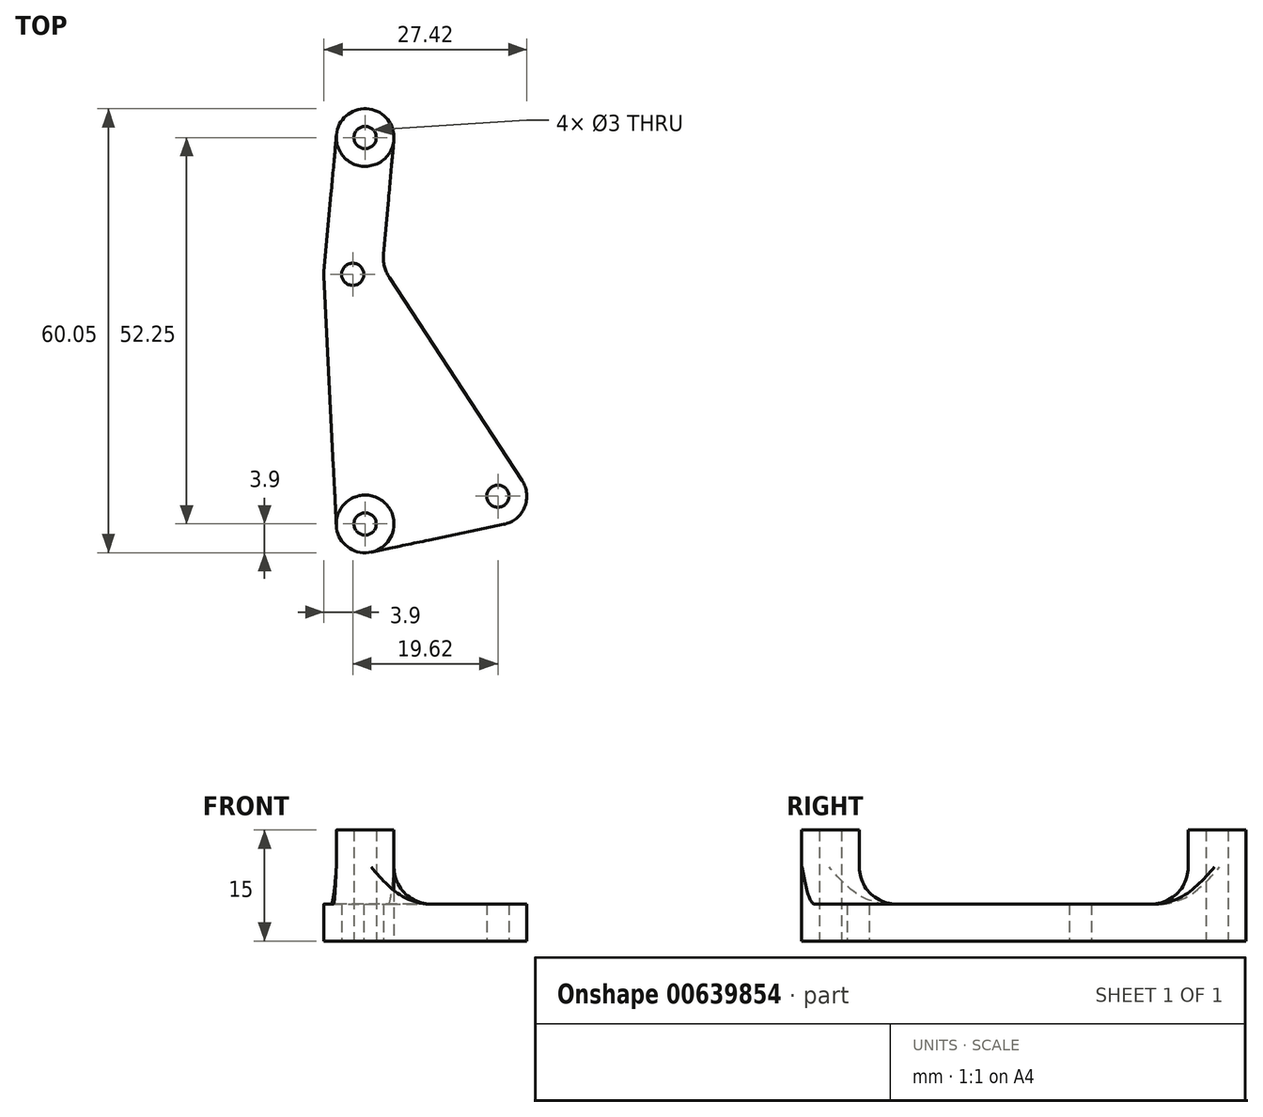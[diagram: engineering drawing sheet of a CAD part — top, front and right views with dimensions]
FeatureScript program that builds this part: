
annotation { "Feature Type Name" : "Feature", "Feature Type Description" : "" }
export const myFeature = defineFeature(function(context is Context, id is Id, definition is map)
    precondition{}
    {
        {
            var Q0;
            Q0=qCreatedBy(makeId("Top.planeOp"),FACE);
            var sketch = newSketch(context, id + "F0", { "sketchPlane" : qUnion([Q0])});
            skCircle(sketch, "E0", {"center": v(-46.5, 15) * mm, "radius": 1.5 * mm});
            skCircle(sketch, "E1", {"center": v(46.5, 15) * mm, "radius": 1.5 * mm});
            skCircle(sketch, "E2", {"center": v(-26.88, -15) * mm, "radius": 1.5 * mm});
            skCircle(sketch, "E3", {"center": v(27.12, -15) * mm, "radius": 1.5 * mm});
            skLineSegment(sketch, "E4.bottom", {"start": v(-47.08, 35.75) * mm, "end": v(47.08, 35.75) * mm, "construction": true});
            skLineSegment(sketch, "E4.top", {"start": v(-47.08, -21) * mm, "end": v(47.07, -21) * mm, "construction": true});
            skLineSegment(sketch, "E4.left", {"start": v(-47.08, 35.75) * mm, "end": v(-47.08, -21) * mm, "construction": true});
            skLineSegment(sketch, "E4.right", {"start": v(47.08, 35.75) * mm, "end": v(47.08, -21) * mm, "construction": true});
            skCircle(sketch, "E5", {"center": v(-44.83, 33.5) * mm, "radius": 1.5 * mm});
            skCircle(sketch, "E6", {"center": v(44.83, 33.5) * mm, "radius": 1.5 * mm});
            skCircle(sketch, "E7", {"center": v(44.82, -18.75) * mm, "radius": 1.5 * mm});
            skCircle(sketch, "E8", {"center": v(-44.83, -18.75) * mm, "radius": 1.5 * mm});
            skCircle(sketch, "E9", {"center": v(-44.83, 33.5) * mm, "radius": 3.9 * mm});
            skCircle(sketch, "E10", {"center": v(44.83, 33.5) * mm, "radius": 3.9 * mm});
            skCircle(sketch, "E11", {"center": v(44.82, -18.75) * mm, "radius": 3.9 * mm});
            skCircle(sketch, "E12", {"center": v(-44.83, -18.75) * mm, "radius": 3.9 * mm});
            skCircle(sketch, "E13", {"center": v(27.12, -15) * mm, "radius": 3.9 * mm, "construction": true});
            skCircle(sketch, "E14", {"center": v(46.5, 15) * mm, "radius": 3.9 * mm, "construction": true});
            skLineSegment(sketch, "E15", {"start": v(-50.4, 14.8) * mm, "end": v(-48.72, -18.94) * mm});
            skLineSegment(sketch, "E16", {"start": v(-42.34, 17.73) * mm, "end": v(-40.94, 33.15) * mm});
            skLineSegment(sketch, "E17", {"start": v(-48.7, 33.85) * mm, "end": v(-50.38, 15.35) * mm});
            skLineSegment(sketch, "E18", {"start": v(-41.54, 14.54) * mm, "end": v(-23.62, -12.87) * mm});
            skArc(sketch, "E19.filletArc", {"start": v(-42.34, 17.73) * mm, "mid": v(-42.2, 16.07) * mm, "end": v(-41.54, 14.54) * mm});
            skLineSegment(sketch, "E20", {"start": v(-44.03, -22.57) * mm, "end": v(-26.08, -18.82) * mm});
            skArc(sketch, "E21", {"start": v(-26.08, -18.82) * mm, "mid": v(-23.28, -16.5) * mm, "end": v(-23.62, -12.87) * mm});
            skArc(sketch, "E22", {"start": v(-23.62, -12.87) * mm, "mid": v(-30.48, -13.5) * mm, "end": v(-26.08, -18.82) * mm, "construction": true});
            skArc(sketch, "E23", {"start": v(-50.4, 14.8) * mm, "mid": v(-42.6, 14.92) * mm, "end": v(-50.38, 15.35) * mm, "construction": true});
            skArc(sketch, "E24", {"start": v(-50.38, 15.35) * mm, "mid": v(-50.4, 15.08) * mm, "end": v(-50.4, 14.8) * mm});
            skSolve(sketch);
        }
        {
            var Q0;
            Q0=makeQuery(id+"F0.imprint","IMPRINT",FACE,{"disambiguationData":[TD([[makeQuery(id+"F0.imprint","IMPRINT",EDGE,{"derivedFrom":sQuery(id+"F0.wireOp",EDGE,"E0")}),-1.0]])]});
            var Q1;
            Q1=makeQuery(id+"F0.imprint","IMPRINT",FACE,{"disambiguationData":[TD([[makeQuery(id+"F0.imprint","IMPRINT",EDGE,{"derivedFrom":sQuery(id+"F0.wireOp",EDGE,"E5")}),-1.0]])]});
            var Q2;
            Q2=makeQuery(id+"F0.imprint","IMPRINT",FACE,{"disambiguationData":[TD([[makeQuery(id+"F0.imprint","IMPRINT",EDGE,{"derivedFrom":sQuery(id+"F0.wireOp",EDGE,"E8")}),-1.0]])]});
            var Q3;
            Q3 = qConstructionFilter(qBodyType(qCreatedBy(id + "F0" ,EDGE), BodyType.WIRE), ConstructionObject.NO);
            extrude(context, id + "F1", {"entities" : qUnion([Q0, Q1, Q2]), "surfaceEntities" : qUnion([Q3]), "depth" : 5 * mm, "offsetDistance" : 25 * mm});
        }
        {
            var Q0;
            Q0=makeQuery(id+"F0.imprint","IMPRINT",FACE,{"disambiguationData":[TD([[makeQuery(id+"F0.imprint","IMPRINT",EDGE,{"derivedFrom":sQuery(id+"F0.wireOp",EDGE,"E5")}),-1.0]])]});
            var Q1;
            Q1=makeQuery(id+"F0.imprint","IMPRINT",FACE,{"disambiguationData":[TD([[makeQuery(id+"F0.imprint","IMPRINT",EDGE,{"derivedFrom":sQuery(id+"F0.wireOp",EDGE,"E8")}),-1.0]])]});
            extrude(context, id + "F2", {"entities" : qUnion([Q0, Q1]), "operationType" : NewBodyOperationType.ADD, "depth" : 15 * mm, "offsetDistance" : 25 * mm});
        }
        {
            var Q0;
            {var subQ0=sQuery(id+"F0.wireOp",EDGE,"E9");Q0=makeQuery(id+"F2.boolean.opBoolean","INTERSECT",EDGE,{"derivedFrom":[makeQuery(id+"F1.opExtrude","CAP_FACE",FACE,{"disambiguationData":[OSD([sQuery(id+"F0.wireOp",EDGE,"E0"),sQuery(id+"F0.wireOp",EDGE,"E2"),sQuery(id+"F0.wireOp",EDGE,"E5"),sQuery(id+"F0.wireOp",EDGE,"E8"),subQ0,sQuery(id+"F0.wireOp",EDGE,"E12"),sQuery(id+"F0.wireOp",EDGE,"E15"),sQuery(id+"F0.wireOp",EDGE,"E16"),sQuery(id+"F0.wireOp",EDGE,"E17"),sQuery(id+"F0.wireOp",EDGE,"E18"),sQuery(id+"F0.wireOp",EDGE,"E19.filletArc"),sQuery(id+"F0.wireOp",EDGE,"E20"),sQuery(id+"F0.wireOp",EDGE,"E21"),sQuery(id+"F0.wireOp",EDGE,"E24")])],"isStart":false}),makeQuery(id+"F2.opExtrude","SWEPT_FACE",FACE,{"disambiguationData":[OSD([subQ0])]})]});}
            var Q1;
            {var subQ0=sQuery(id+"F0.wireOp",EDGE,"E12");Q1=makeQuery(id+"F2.boolean.opBoolean","INTERSECT",EDGE,{"derivedFrom":[makeQuery(id+"F1.opExtrude","CAP_FACE",FACE,{"disambiguationData":[OSD([sQuery(id+"F0.wireOp",EDGE,"E0"),sQuery(id+"F0.wireOp",EDGE,"E2"),sQuery(id+"F0.wireOp",EDGE,"E5"),sQuery(id+"F0.wireOp",EDGE,"E8"),sQuery(id+"F0.wireOp",EDGE,"E9"),subQ0,sQuery(id+"F0.wireOp",EDGE,"E15"),sQuery(id+"F0.wireOp",EDGE,"E16"),sQuery(id+"F0.wireOp",EDGE,"E17"),sQuery(id+"F0.wireOp",EDGE,"E18"),sQuery(id+"F0.wireOp",EDGE,"E19.filletArc"),sQuery(id+"F0.wireOp",EDGE,"E20"),sQuery(id+"F0.wireOp",EDGE,"E21"),sQuery(id+"F0.wireOp",EDGE,"E24")])],"isStart":false}),makeQuery(id+"F2.opExtrude","SWEPT_FACE",FACE,{"disambiguationData":[OSD([subQ0])]})]});}
            fillet(context, id + "F3", {"entities" : qUnion([Q0, Q1]), "radius" : 5 * mm, "tangentPropagation" : true, "allowEdgeOverflow" : false});
        }
    });
